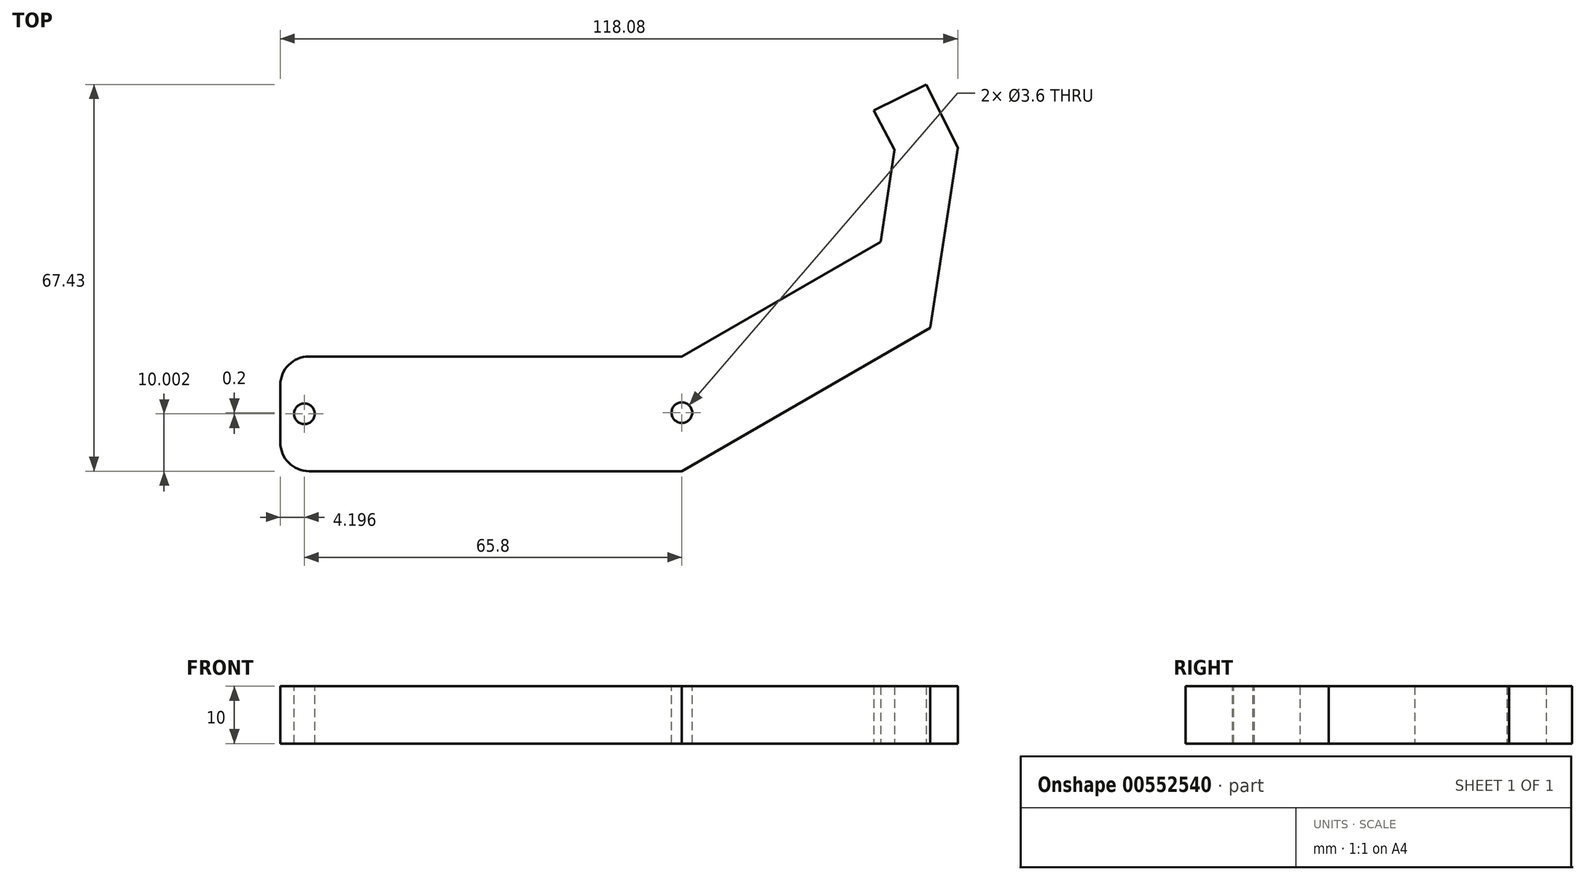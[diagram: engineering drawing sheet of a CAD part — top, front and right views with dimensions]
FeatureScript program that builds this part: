
annotation { "Feature Type Name" : "Feature", "Feature Type Description" : "" }
export const myFeature = defineFeature(function(context is Context, id is Id, definition is map)
    precondition{}
    {
        {
            var Q0;
            Q0=qCreatedBy(makeId("Top.planeOp"),FACE);
            var sketch = newSketch(context, id + "F0", { "sketchPlane" : qUnion([Q0])});
            skLineSegment(sketch, "E0.bottom", {"start": v(-10.9, -3.93) * mm, "end": v(-80.9, -3.93) * mm});
            skLineSegment(sketch, "E0.top", {"start": v(-10.9, 16.07) * mm, "end": v(-80.9, 16.07) * mm});
            skLineSegment(sketch, "E0.left", {"start": v(-10.9, -3.93) * mm, "end": v(-10.9, 16.07) * mm});
            skLineSegment(sketch, "E0.right", {"start": v(-80.9, -3.93) * mm, "end": v(-80.9, 16.07) * mm});
            skPoint(sketch, "E0.middle", {"position": v(-45.9, 6.07) * mm});
            skLineSegment(sketch, "E1", {"start": v(-10.9, 16.07) * mm, "end": v(23.75, 36.07) * mm});
            skLineSegment(sketch, "E2", {"start": v(-10.9, -3.93) * mm, "end": v(32.4, 21.07) * mm});
            skLineSegment(sketch, "E3", {"start": v(23.75, 36.07) * mm, "end": v(32.4, 21.07) * mm});
            skLineSegment(sketch, "E4", {"start": v(32.4, 21.07) * mm, "end": v(37.19, 52.47) * mm});
            skLineSegment(sketch, "E5", {"start": v(23.75, 36.07) * mm, "end": v(26.2, 52.14) * mm});
            skLineSegment(sketch, "E6", {"start": v(26.2, 52.14) * mm, "end": v(37.19, 52.47) * mm});
            skLineSegment(sketch, "E7", {"start": v(37.19, 52.47) * mm, "end": v(31.7, 63.5) * mm});
            skPoint(sketch, "E7.endSnap0", {"position": v(31.7, 52.3) * mm});
            skLineSegment(sketch, "E8", {"start": v(31.7, 63.5) * mm, "end": v(22.56, 58.95) * mm});
            skLineSegment(sketch, "E9", {"start": v(22.56, 58.95) * mm, "end": v(26.2, 52.14) * mm});
            skSolve(sketch);
        }
        {
            var Q0;
            Q0 = qSketchRegion(id + "F0", true);
            extrude(context, id + "F1", {"entities" : qUnion([Q0]), "depth" : 10 * mm, "offsetDistance" : 25 * mm});
        }
        {
            var Q0;
            Q0=makeQuery(id+"F1.opExtrude","SWEPT_EDGE",EDGE,{"disambiguationData":[OSD([sQuery(id+"F0.wireOp",EDGE,"E0.top"),sQuery(id+"F0.wireOp",EDGE,"E0.right")])]});
            var Q1;
            Q1=makeQuery(id+"F1.opExtrude","SWEPT_EDGE",EDGE,{"disambiguationData":[OSD([sQuery(id+"F0.wireOp",EDGE,"E0.bottom"),sQuery(id+"F0.wireOp",EDGE,"E0.right")])]});
            fillet(context, id + "F2", {"entities" : qUnion([Q0, Q1]), "radius" : 5 * mm, "tangentPropagation" : true, "allowEdgeOverflow" : false});
        }
        {
            var Q0;
            Q0=makeQuery(id+"F1.opExtrude","CAP_FACE",FACE,{"disambiguationData":[OSD([sQuery(id+"F0.wireOp",EDGE,"E0.bottom"),sQuery(id+"F0.wireOp",EDGE,"E0.top"),sQuery(id+"F0.wireOp",EDGE,"E0.right"),sQuery(id+"F0.wireOp",EDGE,"E1"),sQuery(id+"F0.wireOp",EDGE,"E2"),sQuery(id+"F0.wireOp",EDGE,"E3")])],"isStart":false});
            var sketch = newSketch(context, id + "F3", { "sketchPlane" : qUnion([Q0])});
            skCircle(sketch, "E10", {"center": v(-76.7, 6.07) * mm, "radius": 1.8 * mm});
            skPoint(sketch, "E10.centerSnap0", {"position": v(-80.9, 6.07) * mm});
            skSolve(sketch);
        }
        {
            var Q0;
            Q0 = qSketchRegion(id + "F3", true);
            extrude(context, id + "F4", {"entities" : qUnion([Q0]), "operationType" : NewBodyOperationType.REMOVE, "oppositeDirection" : true, "depth" : 20 * mm, "offsetDistance" : 25 * mm});
        }
        {
            var Q0;
            Q0=makeQuery(id+"F1.opExtrude","CAP_FACE",FACE,{"disambiguationData":[OSD([sQuery(id+"F0.wireOp",EDGE,"E0.bottom"),sQuery(id+"F0.wireOp",EDGE,"E0.top"),sQuery(id+"F0.wireOp",EDGE,"E0.right"),sQuery(id+"F0.wireOp",EDGE,"E1"),sQuery(id+"F0.wireOp",EDGE,"E2"),sQuery(id+"F0.wireOp",EDGE,"E3")])],"isStart":false});
            var sketch = newSketch(context, id + "F5", { "sketchPlane" : qUnion([Q0])});
            skCircle(sketch, "E11", {"center": v(-10.9, 6.27) * mm, "radius": 1.8 * mm});
            skSolve(sketch);
        }
        {
            var Q0;
            Q0 = qSketchRegion(id + "F5", true);
            extrude(context, id + "F6", {"entities" : qUnion([Q0]), "operationType" : NewBodyOperationType.REMOVE, "oppositeDirection" : true, "depth" : 20 * mm, "offsetDistance" : 25 * mm});
        }
    });
